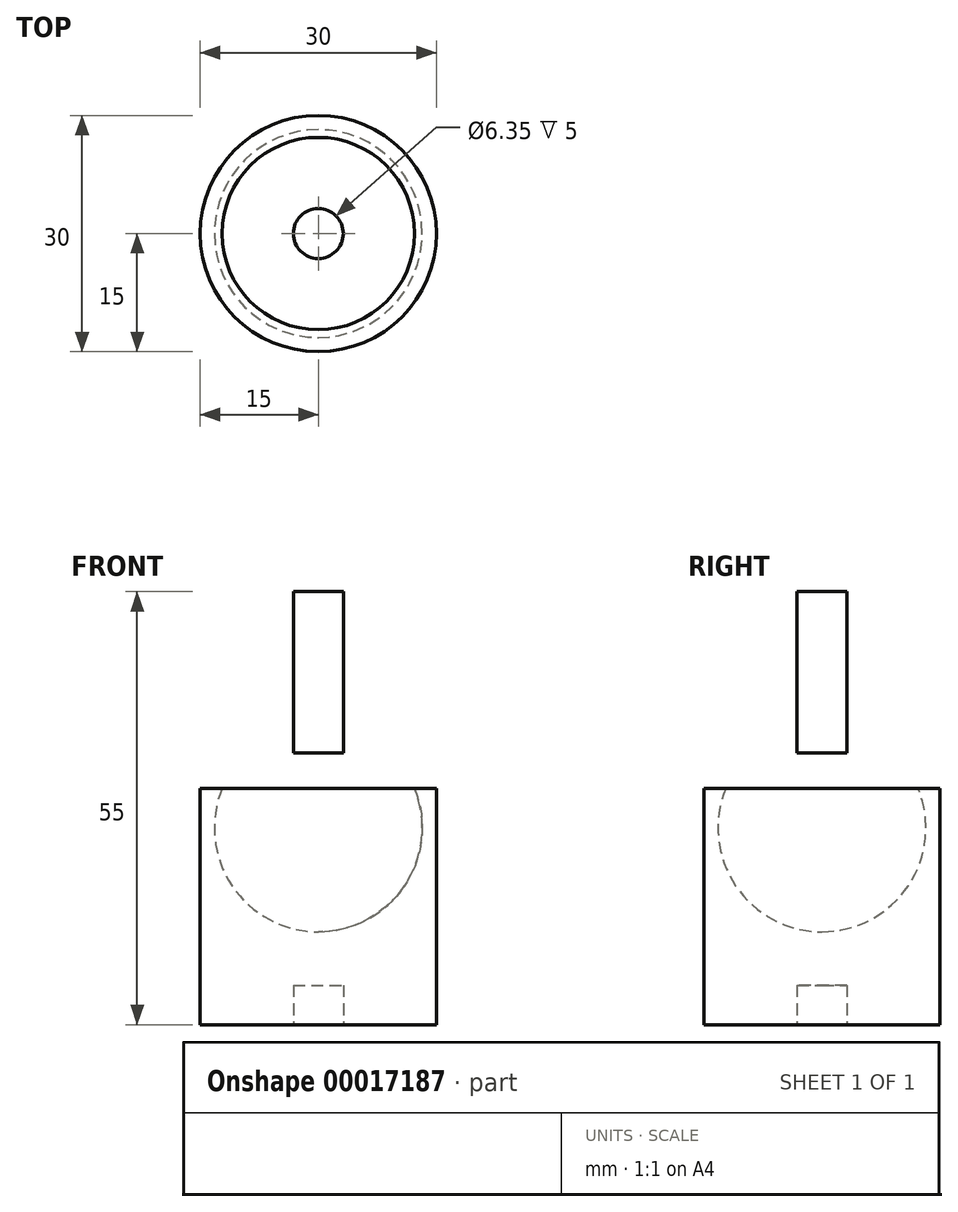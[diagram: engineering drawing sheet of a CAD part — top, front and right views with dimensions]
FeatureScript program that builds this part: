
annotation { "Feature Type Name" : "Feature", "Feature Type Description" : "" }
export const myFeature = defineFeature(function(context is Context, id is Id, definition is map)
    precondition{}
    {
        {
            var Q0;
            Q0=qCreatedBy(makeId("Front.planeOp"),FACE);
            var sketch = newSketch(context, id + "F0", { "sketchPlane" : qUnion([Q0])});
            skLineSegment(sketch, "E0", {"start": v(0, 0) * mm, "end": v(0, 30) * mm});
            skLineSegment(sketch, "E1", {"start": v(0, 30) * mm, "end": v(15, 30) * mm});
            skLineSegment(sketch, "E2", {"start": v(15, 30) * mm, "end": v(15, 0) * mm});
            skLineSegment(sketch, "E3", {"start": v(15, 0) * mm, "end": v(0, 0) * mm});
            skSolve(sketch);
        }
        {
            var Q0;
            Q0 = qSketchRegion(id + "F0", true);
            var Q1;
            Q1=sQuery(id+"F0.wireOp",EDGE,"E0");
            revolve(context, id + "F1", {"entities" : qUnion([Q0]), "axis" : qUnion([Q1]), "revolveType" : RevolveType.FULL});
        }
        {
            var Q0;
            Q0=makeQuery(id+"F1.opRevolve","SWEPT_FACE",FACE,{"disambiguationData":[OSD([sQuery(id+"F0.wireOp",EDGE,"E3")])]});
            var sketch = newSketch(context, id + "F2", { "sketchPlane" : qUnion([Q0])});
            skCircle(sketch, "E4", {"center": v(0, 0) * mm, "radius": 3.17 * mm});
            skSolve(sketch);
        }
        {
            var Q0;
            Q0 = qSketchRegion(id + "F2", true);
            extrude(context, id + "F3", {"entities" : qUnion([Q0]), "operationType" : NewBodyOperationType.REMOVE, "oppositeDirection" : true, "depth" : 5 * mm});
        }
        {
            var Q0;
            Q0=qCreatedBy(makeId("Front.planeOp"),FACE);
            var sketch = newSketch(context, id + "F4", { "sketchPlane" : qUnion([Q0])});
            skLineSegment(sketch, "E5", {"start": v(0, 12) * mm, "end": v(0, 38) * mm});
            skArc(sketch, "E6", {"start": v(0, 12) * mm, "mid": v(13, 25) * mm, "end": v(0, 38) * mm});
            skSolve(sketch);
        }
        {
            var Q0;
            Q0 = qSketchRegion(id + "F4", true);
            var Q1;
            Q1=sQuery(id+"F4.wireOp",EDGE,"E5");
            revolve(context, id + "F5", {"entities" : qUnion([Q0]), "axis" : qUnion([Q1]), "revolveType" : RevolveType.FULL});
        }
        {
            var Q0;
            Q0=qCreatedBy(makeId("Front.planeOp"),FACE);
            var sketch = newSketch(context, id + "F6", { "sketchPlane" : qUnion([Q0])});
            skArc(sketch, "E7.0", {"start": v(0, 11.8) * mm, "mid": v(13.2, 25) * mm, "end": v(0, 38.2) * mm});
            skLineSegment(sketch, "E8", {"start": v(0, 38.2) * mm, "end": v(0, 11.8) * mm});
            skSolve(sketch);
        }
        {
            var Q0;
            Q0 = qSketchRegion(id + "F6", true);
            var Q1;
            Q1=sQuery(id+"F6.wireOp",EDGE,"E8");
            revolve(context, id + "F7", {"operationType" : NewBodyOperationType.REMOVE, "entities" : qUnion([Q0]), "axis" : qUnion([Q1]), "revolveType" : RevolveType.FULL, "oppositeDirection" : true});
        }
        {
            var Q0;
            Q0=qCreatedBy(makeId("Front.planeOp"),FACE);
            var sketch = newSketch(context, id + "F8", { "sketchPlane" : qUnion([Q0])});
            skLineSegment(sketch, "E9", {"start": v(0, 55) * mm, "end": v(3.17, 55) * mm});
            skLineSegment(sketch, "E10", {"start": v(3.17, 55) * mm, "end": v(3.18, 34.54) * mm});
            skLineSegment(sketch, "E11", {"start": v(3.18, 34.54) * mm, "end": v(0, 34.54) * mm});
            skLineSegment(sketch, "E12", {"start": v(0, 34.54) * mm, "end": v(0, 55) * mm});
            skSolve(sketch);
        }
        {
            var Q0;
            Q0 = qSketchRegion(id + "F8", true);
            var Q1;
            Q1=sQuery(id+"F8.wireOp",EDGE,"E12");
            revolve(context, id + "F9", {"operationType" : NewBodyOperationType.ADD, "entities" : qUnion([Q0]), "axis" : qUnion([Q1]), "revolveType" : RevolveType.FULL});
        }
    });
